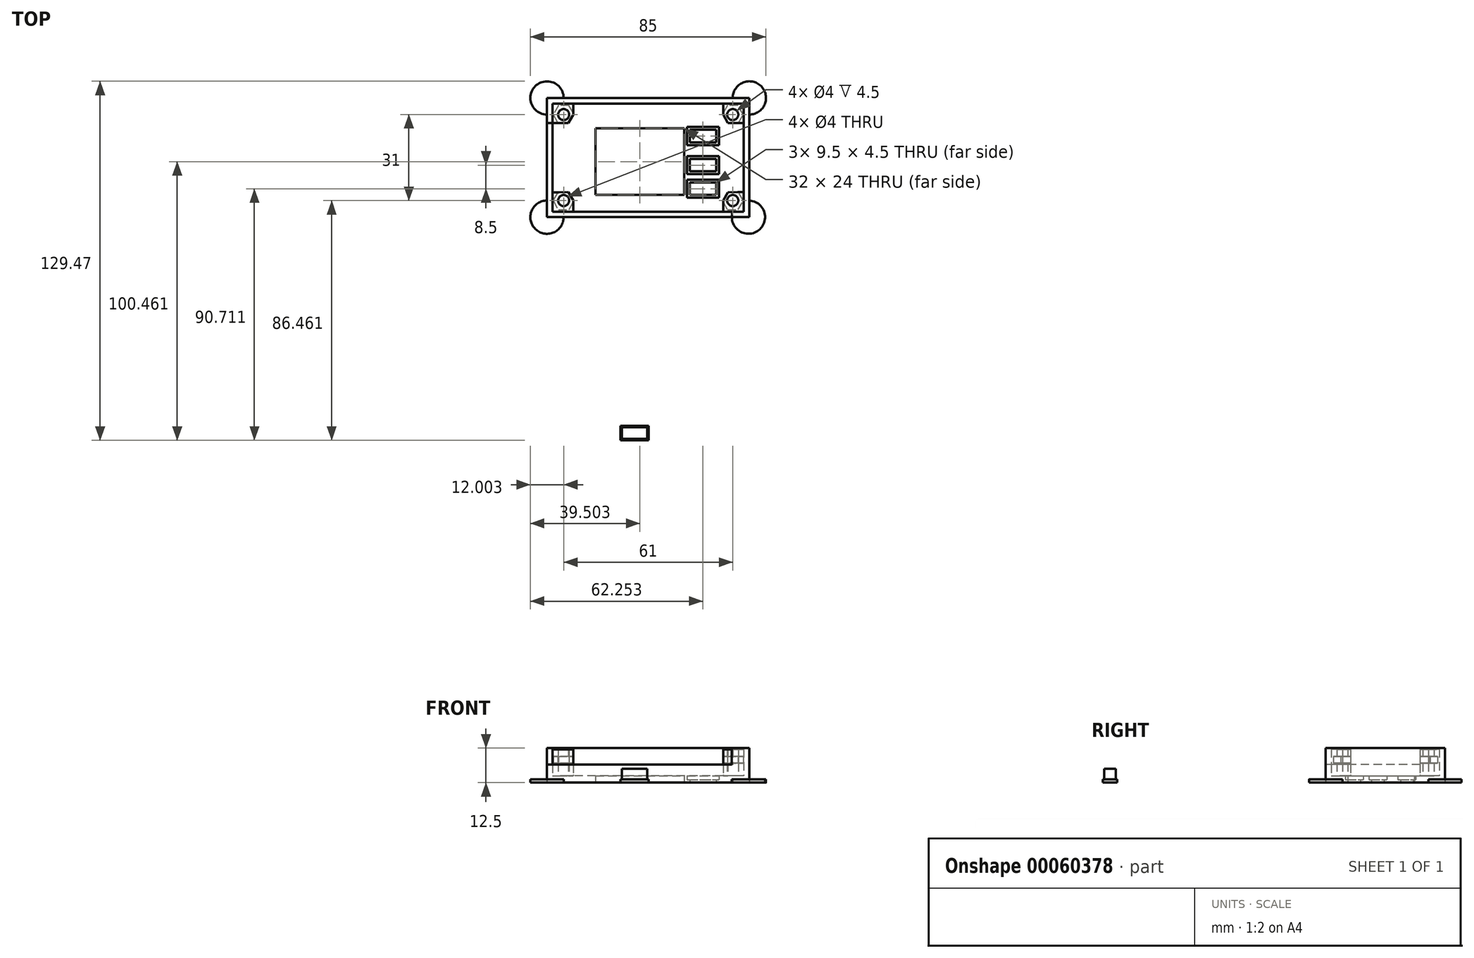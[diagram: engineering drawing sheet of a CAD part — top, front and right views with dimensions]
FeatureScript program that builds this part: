
annotation { "Feature Type Name" : "Feature", "Feature Type Description" : "" }
export const myFeature = defineFeature(function(context is Context, id is Id, definition is map)
    precondition{}
    {
        {
            var Q0;
            Q0=qCreatedBy(makeId("Top.planeOp"),FACE);
            var sketch = newSketch(context, id + "F0", { "sketchPlane" : qUnion([Q0])});
            skCircle(sketch, "E0.cCircle", {"center": v(0, 0) * mm, "radius": 3 * mm, "construction": true});
            skLineSegment(sketch, "E0.0", {"start": v(1.73, 3) * mm, "end": v(3.46, 0) * mm});
            skLineSegment(sketch, "E0.1", {"start": v(3.46, 0) * mm, "end": v(1.74, -3) * mm});
            skLineSegment(sketch, "E0.2", {"start": v(1.74, -3) * mm, "end": v(-1.73, -3) * mm});
            skLineSegment(sketch, "E0.3", {"start": v(-1.73, -3) * mm, "end": v(-3.46, 0) * mm});
            skLineSegment(sketch, "E0.4", {"start": v(-3.46, 0) * mm, "end": v(-1.74, 3) * mm});
            skLineSegment(sketch, "E0.5", {"start": v(-1.74, 3) * mm, "end": v(1.73, 3) * mm});
            skPoint(sketch, "E0.0.midPoint", {"position": v(2.6, 1.5) * mm});
            skCircle(sketch, "E1", {"center": v(0, 0) * mm, "radius": 1.5 * mm});
            skLineSegment(sketch, "E2.bottom", {"start": v(-12.76, 68.41) * mm, "end": v(56.24, 68.41) * mm});
            skLineSegment(sketch, "E2.top", {"start": v(-12.76, 29.41) * mm, "end": v(56.24, 29.41) * mm});
            skLineSegment(sketch, "E2.left", {"start": v(-12.76, 68.41) * mm, "end": v(-12.76, 29.41) * mm});
            skLineSegment(sketch, "E2.right", {"start": v(56.24, 68.41) * mm, "end": v(56.24, 29.41) * mm});
            skPoint(sketch, "E3.0.midPoint", {"position": v(-6.16, 65.92) * mm});
            skLineSegment(sketch, "E3.3", {"start": v(-10.48, 61.4) * mm, "end": v(-12.22, 64.4) * mm, "construction": true});
            skLineSegment(sketch, "E3.2", {"start": v(-7.02, 61.41) * mm, "end": v(-10.48, 61.4) * mm});
            skLineSegment(sketch, "E3.1", {"start": v(-5.3, 64.42) * mm, "end": v(-7.02, 61.41) * mm});
            skLineSegment(sketch, "E3.0", {"start": v(-7.03, 67.41) * mm, "end": v(-5.3, 64.42) * mm, "construction": true});
            skLineSegment(sketch, "E3.4", {"start": v(-12.22, 64.4) * mm, "end": v(-10.5, 67.4) * mm, "construction": true});
            skLineSegment(sketch, "E3.5", {"start": v(-10.5, 67.4) * mm, "end": v(-7.03, 67.41) * mm, "construction": true});
            skCircle(sketch, "E4", {"center": v(-8.76, 64.41) * mm, "radius": 1.5 * mm, "construction": true});
            skCircle(sketch, "E3.cCircle", {"center": v(-8.76, 64.41) * mm, "radius": 3 * mm, "construction": true});
            skPoint(sketch, "E5.0.midPoint", {"position": v(-6.16, 34.92) * mm});
            skLineSegment(sketch, "E5.3", {"start": v(-10.48, 30.4) * mm, "end": v(-12.22, 33.4) * mm, "construction": true});
            skLineSegment(sketch, "E5.2", {"start": v(-7.02, 30.41) * mm, "end": v(-10.48, 30.4) * mm, "construction": true});
            skLineSegment(sketch, "E5.1", {"start": v(-5.3, 33.42) * mm, "end": v(-7.02, 30.41) * mm, "construction": true});
            skLineSegment(sketch, "E5.0", {"start": v(-7.03, 36.41) * mm, "end": v(-5.3, 33.42) * mm});
            skLineSegment(sketch, "E5.4", {"start": v(-12.22, 33.4) * mm, "end": v(-10.5, 36.4) * mm, "construction": true});
            skLineSegment(sketch, "E5.5", {"start": v(-10.5, 36.4) * mm, "end": v(-7.03, 36.41) * mm});
            skCircle(sketch, "E6", {"center": v(-8.76, 33.41) * mm, "radius": 1.5 * mm, "construction": true});
            skCircle(sketch, "E5.cCircle", {"center": v(-8.76, 33.41) * mm, "radius": 3 * mm, "construction": true});
            skPoint(sketch, "E7.0.midPoint", {"position": v(54.84, 65.92) * mm});
            skLineSegment(sketch, "E7.3", {"start": v(50.52, 61.4) * mm, "end": v(48.78, 64.4) * mm});
            skLineSegment(sketch, "E7.2", {"start": v(53.98, 61.41) * mm, "end": v(50.52, 61.4) * mm});
            skLineSegment(sketch, "E7.1", {"start": v(55.7, 64.42) * mm, "end": v(53.98, 61.41) * mm, "construction": true});
            skLineSegment(sketch, "E7.0", {"start": v(53.97, 67.41) * mm, "end": v(55.7, 64.42) * mm, "construction": true});
            skLineSegment(sketch, "E7.4", {"start": v(48.78, 64.4) * mm, "end": v(50.5, 67.4) * mm, "construction": true});
            skLineSegment(sketch, "E7.5", {"start": v(50.5, 67.4) * mm, "end": v(53.97, 67.41) * mm, "construction": true});
            skCircle(sketch, "E8", {"center": v(52.24, 64.41) * mm, "radius": 1.5 * mm, "construction": true});
            skCircle(sketch, "E7.cCircle", {"center": v(52.24, 64.41) * mm, "radius": 3 * mm, "construction": true});
            skPoint(sketch, "E9.0.midPoint", {"position": v(54.84, 34.92) * mm});
            skLineSegment(sketch, "E9.3", {"start": v(50.52, 30.4) * mm, "end": v(48.78, 33.4) * mm, "construction": true});
            skLineSegment(sketch, "E9.2", {"start": v(53.98, 30.41) * mm, "end": v(50.52, 30.4) * mm, "construction": true});
            skLineSegment(sketch, "E9.1", {"start": v(55.7, 33.42) * mm, "end": v(53.98, 30.41) * mm, "construction": true});
            skLineSegment(sketch, "E9.0", {"start": v(53.97, 36.41) * mm, "end": v(55.7, 33.42) * mm, "construction": true});
            skLineSegment(sketch, "E9.4", {"start": v(48.78, 33.4) * mm, "end": v(50.5, 36.4) * mm});
            skLineSegment(sketch, "E9.5", {"start": v(50.5, 36.4) * mm, "end": v(53.97, 36.41) * mm});
            skCircle(sketch, "E10", {"center": v(52.24, 33.41) * mm, "radius": 1.5 * mm, "construction": true});
            skCircle(sketch, "E9.cCircle", {"center": v(52.24, 33.41) * mm, "radius": 3 * mm, "construction": true});
            skLineSegment(sketch, "E11", {"start": v(48.78, 33.4) * mm, "end": v(48.78, 29.41) * mm});
            skLineSegment(sketch, "E12", {"start": v(53.97, 36.41) * mm, "end": v(56.24, 36.41) * mm});
            skCircle(sketch, "E13.0", {"center": v(52.24, 33.41) * mm, "radius": 2 * mm});
            skLineSegment(sketch, "E14.0", {"start": v(50.34, 30.1) * mm, "end": v(48.52, 33.25) * mm});
            skLineSegment(sketch, "E14.1", {"start": v(54.15, 30.11) * mm, "end": v(50.34, 30.1) * mm});
            skLineSegment(sketch, "E14.2", {"start": v(56.05, 33.42) * mm, "end": v(54.15, 30.11) * mm});
            skLineSegment(sketch, "E14.3", {"start": v(54.23, 36.56) * mm, "end": v(56.05, 33.42) * mm});
            skLineSegment(sketch, "E15", {"start": v(-5.3, 33.42) * mm, "end": v(-5.3, 29.41) * mm});
            skLineSegment(sketch, "E16", {"start": v(-10.5, 36.4) * mm, "end": v(-12.76, 36.4) * mm});
            skLineSegment(sketch, "E17", {"start": v(-10.48, 61.4) * mm, "end": v(-12.76, 61.4) * mm});
            skLineSegment(sketch, "E18", {"start": v(-5.3, 64.42) * mm, "end": v(-5.3, 68.41) * mm});
            skLineSegment(sketch, "E19", {"start": v(53.98, 61.41) * mm, "end": v(56.24, 61.42) * mm});
            skLineSegment(sketch, "E20", {"start": v(48.78, 64.4) * mm, "end": v(48.78, 68.41) * mm});
            skCircle(sketch, "E21.0", {"center": v(52.24, 64.41) * mm, "radius": 2 * mm});
            skCircle(sketch, "E22.0", {"center": v(-8.76, 64.41) * mm, "radius": 2 * mm});
            skCircle(sketch, "E23.0", {"center": v(-8.76, 33.41) * mm, "radius": 2 * mm});
            skLineSegment(sketch, "E24.0", {"start": v(-6.86, 67.71) * mm, "end": v(-5.03, 64.57) * mm});
            skLineSegment(sketch, "E24.1", {"start": v(-10.67, 67.7) * mm, "end": v(-6.86, 67.71) * mm});
            skLineSegment(sketch, "E24.2", {"start": v(-12.57, 64.4) * mm, "end": v(-10.67, 67.7) * mm});
            skLineSegment(sketch, "E24.3", {"start": v(-10.74, 61.26) * mm, "end": v(-12.57, 64.4) * mm});
            skLineSegment(sketch, "E25.0", {"start": v(-12.57, 33.4) * mm, "end": v(-10.76, 36.56) * mm});
            skLineSegment(sketch, "E25.1", {"start": v(-10.66, 30.1) * mm, "end": v(-12.57, 33.4) * mm});
            skLineSegment(sketch, "E25.2", {"start": v(-6.85, 30.11) * mm, "end": v(-10.66, 30.1) * mm});
            skLineSegment(sketch, "E25.3", {"start": v(-5.03, 33.27) * mm, "end": v(-6.85, 30.11) * mm});
            skLineSegment(sketch, "E26.0", {"start": v(56.05, 64.42) * mm, "end": v(50.35, 54.5) * mm});
            skLineSegment(sketch, "E26.1", {"start": v(54.14, 67.71) * mm, "end": v(56.05, 64.42) * mm});
            skLineSegment(sketch, "E26.2", {"start": v(50.33, 67.7) * mm, "end": v(54.14, 67.71) * mm});
            skLineSegment(sketch, "E26.3", {"start": v(48.52, 64.55) * mm, "end": v(50.33, 67.7) * mm});
            skPoint(sketch, "E27", {"position": v(2.74, 35.41) * mm});
            skLineSegment(sketch, "E28.bottom", {"start": v(2.74, 35.41) * mm, "end": v(34.74, 35.41) * mm});
            skLineSegment(sketch, "E28.top", {"start": v(2.74, 59.41) * mm, "end": v(34.74, 59.41) * mm});
            skLineSegment(sketch, "E28.left", {"start": v(2.74, 35.41) * mm, "end": v(2.74, 59.41) * mm});
            skLineSegment(sketch, "E28.right", {"start": v(34.74, 35.41) * mm, "end": v(34.74, 59.41) * mm});
            skPoint(sketch, "E29", {"position": v(36.74, 59.41) * mm});
            skLineSegment(sketch, "E30.bottom", {"start": v(36.74, 59.41) * mm, "end": v(46.24, 59.41) * mm, "construction": true});
            skLineSegment(sketch, "E30.top", {"start": v(36.74, 54.91) * mm, "end": v(46.24, 54.91) * mm, "construction": true});
            skLineSegment(sketch, "E30.left", {"start": v(36.74, 59.41) * mm, "end": v(36.74, 54.91) * mm, "construction": true});
            skLineSegment(sketch, "E30.right", {"start": v(46.24, 59.41) * mm, "end": v(46.24, 54.91) * mm, "construction": true});
            skLineSegment(sketch, "E31.bottom", {"start": v(36.74, 35.41) * mm, "end": v(46.24, 35.41) * mm});
            skLineSegment(sketch, "E31.top", {"start": v(36.74, 39.91) * mm, "end": v(46.24, 39.91) * mm});
            skLineSegment(sketch, "E31.left", {"start": v(36.74, 35.41) * mm, "end": v(36.74, 39.91) * mm});
            skLineSegment(sketch, "E31.right", {"start": v(46.24, 35.41) * mm, "end": v(46.24, 39.91) * mm});
            skLineSegment(sketch, "E32.bottom", {"start": v(36.74, 43.91) * mm, "end": v(46.24, 43.91) * mm});
            skLineSegment(sketch, "E32.top", {"start": v(36.74, 48.41) * mm, "end": v(46.24, 48.41) * mm});
            skLineSegment(sketch, "E32.left", {"start": v(36.74, 43.91) * mm, "end": v(36.74, 48.41) * mm});
            skLineSegment(sketch, "E32.right", {"start": v(46.24, 43.91) * mm, "end": v(46.24, 48.41) * mm});
            skLineSegment(sketch, "E33.0", {"start": v(-14.76, 70.41) * mm, "end": v(-14.76, 27.41) * mm});
            skLineSegment(sketch, "E33.1", {"start": v(-14.76, 70.41) * mm, "end": v(58.24, 70.41) * mm});
            skLineSegment(sketch, "E33.2", {"start": v(58.24, 70.41) * mm, "end": v(58.24, 27.41) * mm});
            skLineSegment(sketch, "E33.3", {"start": v(-14.76, 27.41) * mm, "end": v(58.24, 27.41) * mm});
            skPoint(sketch, "E34", {"position": v(-14.76, 61.41) * mm});
            skLineSegment(sketch, "E35", {"start": v(-14.76, 61.41) * mm, "end": v(-12.76, 61.41) * mm});
            skLineSegment(sketch, "E36.bottom", {"start": v(13.09, -34.33) * mm, "end": v(22.29, -34.33) * mm});
            skLineSegment(sketch, "E36.top", {"start": v(13.09, -38.53) * mm, "end": v(22.29, -38.53) * mm});
            skLineSegment(sketch, "E36.left", {"start": v(13.09, -34.33) * mm, "end": v(13.09, -38.53) * mm});
            skLineSegment(sketch, "E36.right", {"start": v(22.29, -34.33) * mm, "end": v(22.29, -38.53) * mm});
            skLineSegment(sketch, "E37.0", {"start": v(12.09, -33.33) * mm, "end": v(23.29, -33.33) * mm});
            skLineSegment(sketch, "E37.1", {"start": v(12.09, -33.33) * mm, "end": v(12.09, -39.53) * mm});
            skLineSegment(sketch, "E37.2", {"start": v(12.09, -39.53) * mm, "end": v(23.29, -39.53) * mm});
            skLineSegment(sketch, "E37.3", {"start": v(23.29, -33.33) * mm, "end": v(23.29, -39.53) * mm});
            skLineSegment(sketch, "E38.bottom", {"start": v(12.2, -48.35) * mm, "end": v(21.4, -48.35) * mm});
            skLineSegment(sketch, "E38.top", {"start": v(12.2, -52.55) * mm, "end": v(21.4, -52.55) * mm});
            skLineSegment(sketch, "E38.left", {"start": v(12.2, -48.35) * mm, "end": v(12.2, -52.55) * mm});
            skLineSegment(sketch, "E38.right", {"start": v(21.4, -48.35) * mm, "end": v(21.4, -52.55) * mm});
            skLineSegment(sketch, "E39.0", {"start": v(11.7, -47.85) * mm, "end": v(21.9, -47.85) * mm});
            skLineSegment(sketch, "E39.1", {"start": v(11.7, -47.85) * mm, "end": v(11.7, -53.05) * mm});
            skLineSegment(sketch, "E39.2", {"start": v(11.7, -53.05) * mm, "end": v(21.9, -53.05) * mm});
            skLineSegment(sketch, "E39.3", {"start": v(21.9, -47.85) * mm, "end": v(21.9, -53.05) * mm});
            skArc(sketch, "E40", {"start": v(58.24, 64.42) * mm, "mid": v(62.48, 74.66) * mm, "end": v(52.24, 70.41) * mm});
            skArc(sketch, "E41", {"start": v(52.24, 29.41) * mm, "mid": v(61.24, 22.44) * mm, "end": v(58.24, 33.42) * mm});
            skArc(sketch, "E42", {"start": v(-14.76, 33.4) * mm, "mid": v(-19, 23.16) * mm, "end": v(-8.76, 27.41) * mm});
            skArc(sketch, "E43", {"start": v(-8.76, 70.41) * mm, "mid": v(-19, 74.64) * mm, "end": v(-14.76, 64.4) * mm});
            skLineSegment(sketch, "E44.0", {"start": v(35.74, 53.91) * mm, "end": v(47.24, 53.91) * mm, "construction": true});
            skLineSegment(sketch, "E44.1", {"start": v(35.74, 60.41) * mm, "end": v(35.74, 53.91) * mm, "construction": true});
            skLineSegment(sketch, "E44.2", {"start": v(35.74, 60.41) * mm, "end": v(47.24, 60.41) * mm, "construction": true});
            skLineSegment(sketch, "E44.3", {"start": v(47.24, 60.41) * mm, "end": v(47.24, 53.91) * mm, "construction": true});
            skLineSegment(sketch, "E45.0", {"start": v(35.74, 49.41) * mm, "end": v(47.24, 49.41) * mm});
            skLineSegment(sketch, "E45.1", {"start": v(35.74, 42.91) * mm, "end": v(35.74, 49.41) * mm});
            skLineSegment(sketch, "E45.2", {"start": v(35.74, 42.91) * mm, "end": v(47.24, 42.91) * mm});
            skLineSegment(sketch, "E45.3", {"start": v(47.24, 42.91) * mm, "end": v(47.24, 49.41) * mm});
            skLineSegment(sketch, "E46.0", {"start": v(35.74, 40.91) * mm, "end": v(47.24, 40.91) * mm});
            skLineSegment(sketch, "E46.1", {"start": v(35.74, 34.41) * mm, "end": v(35.74, 40.91) * mm});
            skLineSegment(sketch, "E46.2", {"start": v(35.74, 34.41) * mm, "end": v(47.24, 34.41) * mm});
            skLineSegment(sketch, "E46.3", {"start": v(47.24, 34.41) * mm, "end": v(47.24, 40.91) * mm});
            skLineSegment(sketch, "E47.bottom", {"start": v(36.74, 54.41) * mm, "end": v(46.24, 54.41) * mm});
            skLineSegment(sketch, "E47.top", {"start": v(36.74, 58.91) * mm, "end": v(46.24, 58.91) * mm});
            skLineSegment(sketch, "E47.left", {"start": v(36.74, 54.41) * mm, "end": v(36.74, 58.91) * mm});
            skLineSegment(sketch, "E47.right", {"start": v(46.24, 54.41) * mm, "end": v(46.24, 58.91) * mm});
            skLineSegment(sketch, "E48.0", {"start": v(35.74, 59.91) * mm, "end": v(47.24, 59.91) * mm});
            skLineSegment(sketch, "E48.1", {"start": v(35.74, 53.41) * mm, "end": v(35.74, 59.91) * mm});
            skLineSegment(sketch, "E48.2", {"start": v(35.74, 53.41) * mm, "end": v(47.24, 53.41) * mm});
            skLineSegment(sketch, "E48.3", {"start": v(47.24, 53.41) * mm, "end": v(47.24, 59.91) * mm});
            skSolve(sketch);
        }
        {
            var Q0;
            {var subQ14=sQuery(id+"F0.wireOp",EDGE,"E3.2");Q0=makeQuery(id+"F0.imprint","IMPRINT",FACE,{"disambiguationData":[TD([[makeQuery(id+"F0.imprint","IMPRINT",EDGE,{"derivedFrom":subQ14}),1.0]])]});}
            var Q1;
            Q1=makeQuery(id+"F0.imprint","IMPRINT",FACE,{"disambiguationData":[TD([[makeQuery(id+"F0.imprint","IMPRINT",EDGE,{"derivedFrom":sQuery(id+"F0.wireOp",EDGE,"E22.0")}),1.0]])]});
            var Q2;
            Q2=makeQuery(id+"F0.imprint","IMPRINT",FACE,{"disambiguationData":[TD([[makeQuery(id+"F0.imprint","IMPRINT",EDGE,{"derivedFrom":sQuery(id+"F0.wireOp",EDGE,"E21.0")}),1.0]])]});
            var Q3;
            Q3=makeQuery(id+"F0.imprint","IMPRINT",FACE,{"disambiguationData":[TD([[makeQuery(id+"F0.imprint","IMPRINT",EDGE,{"derivedFrom":sQuery(id+"F0.wireOp",EDGE,"E13.0")}),1.0]])]});
            var Q4;
            Q4=makeQuery(id+"F0.imprint","IMPRINT",FACE,{"disambiguationData":[TD([[makeQuery(id+"F0.imprint","IMPRINT",EDGE,{"derivedFrom":sQuery(id+"F0.wireOp",EDGE,"E23.0")}),1.0]])]});
            var Q5;
            {var subQ12=sQuery(id+"F0.wireOp",EDGE,"E25.1");Q5=makeQuery(id+"F0.imprint","IMPRINT",FACE,{"disambiguationData":[TD([[makeQuery(id+"F0.imprint","IMPRINT",EDGE,{"derivedFrom":subQ12}),1.0]])]});}
            var Q6;
            {var subQ1=sQuery(id+"F0.wireOp",EDGE,"E5.0");Q6=makeQuery(id+"F0.imprint","IMPRINT",FACE,{"disambiguationData":[TD([[makeQuery(id+"F0.imprint","IMPRINT",EDGE,{"derivedFrom":subQ1}),-1.0]])]});}
            var Q7;
            {var subQ0=sQuery(id+"F0.wireOp",EDGE,"E35");Q7=makeQuery(id+"F0.imprint","IMPRINT",FACE,{"disambiguationData":[TD([[makeQuery(id+"F0.imprint","IMPRINT",EDGE,{"derivedFrom":subQ0}),-1.0]])]});}
            var Q8;
            {var subQ0=sQuery(id+"F0.wireOp",EDGE,"E35");Q8=makeQuery(id+"F0.imprint","IMPRINT",FACE,{"disambiguationData":[TD([[makeQuery(id+"F0.imprint","IMPRINT",EDGE,{"derivedFrom":subQ0}),-1.0]])]});}
            var Q9;
            {var subQ12=sQuery(id+"F0.wireOp",EDGE,"E24.1");Q9=makeQuery(id+"F0.imprint","IMPRINT",FACE,{"disambiguationData":[TD([[makeQuery(id+"F0.imprint","IMPRINT",EDGE,{"derivedFrom":subQ12}),1.0]])]});}
            var Q10;
            {var subQ6=sQuery(id+"F0.wireOp",EDGE,"E3.2");Q10=makeQuery(id+"F0.imprint","IMPRINT",FACE,{"disambiguationData":[TD([[makeQuery(id+"F0.imprint","IMPRINT",EDGE,{"derivedFrom":subQ6}),-1.0]])]});}
            var Q11;
            {var subQ13=sQuery(id+"F0.wireOp",EDGE,"E14.1");Q11=makeQuery(id+"F0.imprint","IMPRINT",FACE,{"disambiguationData":[TD([[makeQuery(id+"F0.imprint","IMPRINT",EDGE,{"derivedFrom":subQ13}),1.0]])]});}
            var Q12;
            {var subQ5=sQuery(id+"F0.wireOp",EDGE,"E26.1");Q12=makeQuery(id+"F0.imprint","IMPRINT",FACE,{"disambiguationData":[TD([[makeQuery(id+"F0.imprint","IMPRINT",EDGE,{"derivedFrom":subQ5}),1.0]])]});}
            var Q13;
            {var subQ1=sQuery(id+"F0.wireOp",EDGE,"E7.3");Q13=makeQuery(id+"F0.imprint","IMPRINT",FACE,{"disambiguationData":[TD([[makeQuery(id+"F0.imprint","IMPRINT",EDGE,{"derivedFrom":subQ1}),-1.0]])]});}
            var Q14;
            {var subQ17=sQuery(id+"F0.wireOp",EDGE,"E35");Q14=makeQuery(id+"F0.imprint","IMPRINT",FACE,{"disambiguationData":[TD([[makeQuery(id+"F0.imprint","IMPRINT",EDGE,{"derivedFrom":subQ17}),1.0]])]});}
            var Q15;
            {var subQ4=sQuery(id+"F0.wireOp",EDGE,"E9.4");Q15=makeQuery(id+"F0.imprint","IMPRINT",FACE,{"disambiguationData":[TD([[makeQuery(id+"F0.imprint","IMPRINT",EDGE,{"derivedFrom":subQ4}),-1.0]])]});}
            extrude(context, id + "F1", {"entities" : qUnion([Q0, Q1, Q2, Q3, Q4, Q5, Q6, Q7, Q8, Q9, Q10, Q11, Q12, Q13, Q14, Q15]), "depth" : 2.5 * mm});
        }
        {
            var Q0;
            Q0=makeQuery(id+"F0.imprint","IMPRINT",FACE,{"disambiguationData":[TD([[makeQuery(id+"F0.imprint","IMPRINT",EDGE,{"derivedFrom":sQuery(id+"F0.wireOp",EDGE,"E30.bottom")}),1.0]])]});
            var Q1;
            Q1=makeQuery(id+"F0.imprint","IMPRINT",FACE,{"disambiguationData":[TD([[makeQuery(id+"F0.imprint","IMPRINT",EDGE,{"derivedFrom":sQuery(id+"F0.wireOp",EDGE,"E32.bottom")}),-1.0]])]});
            var Q2;
            Q2=makeQuery(id+"F0.imprint","IMPRINT",FACE,{"disambiguationData":[TD([[makeQuery(id+"F0.imprint","IMPRINT",EDGE,{"derivedFrom":sQuery(id+"F0.wireOp",EDGE,"E31.bottom")}),-1.0]])]});
            var Q3;
            Q3=makeQuery(id+"F0.imprint","IMPRINT",FACE,{"disambiguationData":[TD([[makeQuery(id+"F0.imprint","IMPRINT",EDGE,{"derivedFrom":sQuery(id+"F0.wireOp",EDGE,"E47.bottom")}),-1.0]])]});
            extrude(context, id + "F2", {"entities" : qUnion([Q0, Q1, Q2, Q3]), "operationType" : NewBodyOperationType.ADD, "depth" : 1 * mm});
        }
        {
            var Q0;
            {var subQ12=sQuery(id+"F0.wireOp",EDGE,"E14.1");Q0=makeQuery(id+"F0.imprint","IMPRINT",FACE,{"disambiguationData":[TD([[makeQuery(id+"F0.imprint","IMPRINT",EDGE,{"derivedFrom":subQ12}),1.0]])]});}
            var Q1;
            {var subQ6=sQuery(id+"F0.wireOp",EDGE,"E9.4");Q1=makeQuery(id+"F0.imprint","IMPRINT",FACE,{"disambiguationData":[TD([[makeQuery(id+"F0.imprint","IMPRINT",EDGE,{"derivedFrom":subQ6}),-1.0]])]});}
            var Q2;
            {var subQ5=sQuery(id+"F0.wireOp",EDGE,"E25.1");Q2=makeQuery(id+"F0.imprint","IMPRINT",FACE,{"disambiguationData":[TD([[makeQuery(id+"F0.imprint","IMPRINT",EDGE,{"derivedFrom":subQ5}),1.0]])]});}
            var Q3;
            {var subQ5=sQuery(id+"F0.wireOp",EDGE,"E5.0");Q3=makeQuery(id+"F0.imprint","IMPRINT",FACE,{"disambiguationData":[TD([[makeQuery(id+"F0.imprint","IMPRINT",EDGE,{"derivedFrom":subQ5}),-1.0]])]});}
            var Q4;
            {var subQ11=sQuery(id+"F0.wireOp",EDGE,"E24.1");Q4=makeQuery(id+"F0.imprint","IMPRINT",FACE,{"disambiguationData":[TD([[makeQuery(id+"F0.imprint","IMPRINT",EDGE,{"derivedFrom":subQ11}),1.0]])]});}
            var Q5;
            {var subQ5=sQuery(id+"F0.wireOp",EDGE,"E3.2");Q5=makeQuery(id+"F0.imprint","IMPRINT",FACE,{"disambiguationData":[TD([[makeQuery(id+"F0.imprint","IMPRINT",EDGE,{"derivedFrom":subQ5}),-1.0]])]});}
            var Q6;
            {var subQ7=sQuery(id+"F0.wireOp",EDGE,"E26.1");Q6=makeQuery(id+"F0.imprint","IMPRINT",FACE,{"disambiguationData":[TD([[makeQuery(id+"F0.imprint","IMPRINT",EDGE,{"derivedFrom":subQ7}),1.0]])]});}
            var Q7;
            {var subQ1=sQuery(id+"F0.wireOp",EDGE,"E7.3");Q7=makeQuery(id+"F0.imprint","IMPRINT",FACE,{"disambiguationData":[TD([[makeQuery(id+"F0.imprint","IMPRINT",EDGE,{"derivedFrom":subQ1}),-1.0]])]});}
            extrude(context, id + "F3", {"entities" : qUnion([Q0, Q1, Q2, Q3, Q4, Q5, Q6, Q7]), "operationType" : NewBodyOperationType.ADD, "depth" : 7 * mm});
        }
        {
            var Q0;
            {var subQ12=sQuery(id+"F0.wireOp",EDGE,"E14.1");Q0=makeQuery(id+"F0.imprint","IMPRINT",FACE,{"disambiguationData":[TD([[makeQuery(id+"F0.imprint","IMPRINT",EDGE,{"derivedFrom":subQ12}),1.0]])]});}
            var Q1;
            {var subQ7=sQuery(id+"F0.wireOp",EDGE,"E26.1");Q1=makeQuery(id+"F0.imprint","IMPRINT",FACE,{"disambiguationData":[TD([[makeQuery(id+"F0.imprint","IMPRINT",EDGE,{"derivedFrom":subQ7}),1.0]])]});}
            var Q2;
            {var subQ11=sQuery(id+"F0.wireOp",EDGE,"E24.1");Q2=makeQuery(id+"F0.imprint","IMPRINT",FACE,{"disambiguationData":[TD([[makeQuery(id+"F0.imprint","IMPRINT",EDGE,{"derivedFrom":subQ11}),1.0]])]});}
            var Q3;
            {var subQ5=sQuery(id+"F0.wireOp",EDGE,"E25.1");Q3=makeQuery(id+"F0.imprint","IMPRINT",FACE,{"disambiguationData":[TD([[makeQuery(id+"F0.imprint","IMPRINT",EDGE,{"derivedFrom":subQ5}),1.0]])]});}
            extrude(context, id + "F4", {"entities" : qUnion([Q0, Q1, Q2, Q3]), "operationType" : NewBodyOperationType.ADD, "endBound" : BoundingType.UP_TO_NEXT, "depth" : 25 * mm});
        }
        {
            var Q0;
            Q0=makeQuery(id+"F4.opExtrude","CAP_FACE",FACE,{"disambiguationData":[OSD([sQuery(id+"F0.wireOp",EDGE,"E2.top"),sQuery(id+"F0.wireOp",EDGE,"E2.right"),sQuery(id+"F0.wireOp",EDGE,"E9.4"),sQuery(id+"F0.wireOp",EDGE,"E9.5"),sQuery(id+"F0.wireOp",EDGE,"E11"),sQuery(id+"F0.wireOp",EDGE,"E12"),sQuery(id+"F0.wireOp",EDGE,"E13.0")])],"isStart":false});
            var Q1;
            Q1=makeQuery(id+"F4.opExtrude","CAP_FACE",FACE,{"disambiguationData":[OSD([sQuery(id+"F0.wireOp",EDGE,"E2.top"),sQuery(id+"F0.wireOp",EDGE,"E2.left"),sQuery(id+"F0.wireOp",EDGE,"E5.0"),sQuery(id+"F0.wireOp",EDGE,"E5.5"),sQuery(id+"F0.wireOp",EDGE,"E15"),sQuery(id+"F0.wireOp",EDGE,"E16"),sQuery(id+"F0.wireOp",EDGE,"E23.0")])],"isStart":false});
            var Q2;
            Q2=makeQuery(id+"F4.opExtrude","CAP_FACE",FACE,{"disambiguationData":[OSD([sQuery(id+"F0.wireOp",EDGE,"E2.bottom"),sQuery(id+"F0.wireOp",EDGE,"E2.left"),sQuery(id+"F0.wireOp",EDGE,"E3.2"),sQuery(id+"F0.wireOp",EDGE,"E3.1"),sQuery(id+"F0.wireOp",EDGE,"E17"),sQuery(id+"F0.wireOp",EDGE,"E18"),sQuery(id+"F0.wireOp",EDGE,"E22.0")])],"isStart":false});
            var Q3;
            Q3=makeQuery(id+"F4.opExtrude","CAP_FACE",FACE,{"disambiguationData":[OSD([sQuery(id+"F0.wireOp",EDGE,"E2.bottom"),sQuery(id+"F0.wireOp",EDGE,"E2.right"),sQuery(id+"F0.wireOp",EDGE,"E7.3"),sQuery(id+"F0.wireOp",EDGE,"E7.2"),sQuery(id+"F0.wireOp",EDGE,"E19"),sQuery(id+"F0.wireOp",EDGE,"E20"),sQuery(id+"F0.wireOp",EDGE,"E21.0")])],"isStart":false});
            var Q4;
            {var subQ13=sQuery(id+"F0.wireOp",EDGE,"E14.1");Q4=makeQuery(id+"F0.imprint","IMPRINT",FACE,{"disambiguationData":[TD([[makeQuery(id+"F0.imprint","IMPRINT",EDGE,{"derivedFrom":subQ13}),1.0]])]});}
            var Q5;
            {var subQ5=sQuery(id+"F0.wireOp",EDGE,"E26.1");Q5=makeQuery(id+"F0.imprint","IMPRINT",FACE,{"disambiguationData":[TD([[makeQuery(id+"F0.imprint","IMPRINT",EDGE,{"derivedFrom":subQ5}),1.0]])]});}
            var Q6;
            {var subQ12=sQuery(id+"F0.wireOp",EDGE,"E24.1");Q6=makeQuery(id+"F0.imprint","IMPRINT",FACE,{"disambiguationData":[TD([[makeQuery(id+"F0.imprint","IMPRINT",EDGE,{"derivedFrom":subQ12}),1.0]])]});}
            var Q7;
            {var subQ12=sQuery(id+"F0.wireOp",EDGE,"E25.1");Q7=makeQuery(id+"F0.imprint","IMPRINT",FACE,{"disambiguationData":[TD([[makeQuery(id+"F0.imprint","IMPRINT",EDGE,{"derivedFrom":subQ12}),1.0]])]});}
            extrude(context, id + "F5", {"entities" : qUnion([Q0, Q1, Q2, Q3, Q4, Q5, Q6, Q7]), "operationType" : NewBodyOperationType.ADD, "depth" : 12 * mm});
        }
        {
            var Q0;
            Q0=makeQuery(id+"F3.opExtrude","CAP_FACE",FACE,{"disambiguationData":[OSD([sQuery(id+"F0.wireOp",EDGE,"E2.top"),sQuery(id+"F0.wireOp",EDGE,"E2.right"),sQuery(id+"F0.wireOp",EDGE,"E9.4"),sQuery(id+"F0.wireOp",EDGE,"E9.5"),sQuery(id+"F0.wireOp",EDGE,"E11"),sQuery(id+"F0.wireOp",EDGE,"E12"),sQuery(id+"F0.wireOp",EDGE,"E13.0")])],"isStart":false});
            var Q1;
            Q1=makeQuery(id+"F3.opExtrude","CAP_FACE",FACE,{"disambiguationData":[OSD([sQuery(id+"F0.wireOp",EDGE,"E2.top"),sQuery(id+"F0.wireOp",EDGE,"E2.left"),sQuery(id+"F0.wireOp",EDGE,"E5.0"),sQuery(id+"F0.wireOp",EDGE,"E5.5"),sQuery(id+"F0.wireOp",EDGE,"E15"),sQuery(id+"F0.wireOp",EDGE,"E16"),sQuery(id+"F0.wireOp",EDGE,"E23.0")])],"isStart":false});
            var Q2;
            Q2=makeQuery(id+"F3.opExtrude","CAP_FACE",FACE,{"disambiguationData":[OSD([sQuery(id+"F0.wireOp",EDGE,"E2.bottom"),sQuery(id+"F0.wireOp",EDGE,"E2.left"),sQuery(id+"F0.wireOp",EDGE,"E3.2"),sQuery(id+"F0.wireOp",EDGE,"E3.1"),sQuery(id+"F0.wireOp",EDGE,"E17"),sQuery(id+"F0.wireOp",EDGE,"E18"),sQuery(id+"F0.wireOp",EDGE,"E22.0")])],"isStart":false});
            var Q3;
            Q3=makeQuery(id+"F3.opExtrude","CAP_FACE",FACE,{"disambiguationData":[OSD([sQuery(id+"F0.wireOp",EDGE,"E2.bottom"),sQuery(id+"F0.wireOp",EDGE,"E2.right"),sQuery(id+"F0.wireOp",EDGE,"E7.3"),sQuery(id+"F0.wireOp",EDGE,"E7.2"),sQuery(id+"F0.wireOp",EDGE,"E19"),sQuery(id+"F0.wireOp",EDGE,"E20"),sQuery(id+"F0.wireOp",EDGE,"E21.0")])],"isStart":false});
            extrude(context, id + "F6", {"entities" : qUnion([Q0, Q1, Q2, Q3]), "operationType" : NewBodyOperationType.ADD, "depth" : 5 * mm, "hasSecondDirection" : true, "secondDirectionOppositeDirection" : false, "secondDirectionDepth" : 2.5 * mm});
        }
        {
            var Q0;
            {var subQ18=sQuery(id+"F0.wireOp",EDGE,"E33.1");Q0=makeQuery(id+"F0.imprint","IMPRINT",FACE,{"disambiguationData":[TD([[makeQuery(id+"F0.imprint","IMPRINT",EDGE,{"derivedFrom":subQ18}),-1.0]])]});}
            var Q1;
            {var subQ0=sQuery(id+"F0.wireOp",EDGE,"E35");Q1=makeQuery(id+"F0.imprint","IMPRINT",FACE,{"disambiguationData":[TD([[makeQuery(id+"F0.imprint","IMPRINT",EDGE,{"derivedFrom":subQ0}),-1.0]])]});}
            extrude(context, id + "F7", {"entities" : qUnion([Q0, Q1]), "operationType" : NewBodyOperationType.ADD, "depth" : 12.5 * mm});
        }
        {
            var Q0;
            {var subQ0=sQuery(id+"F0.wireOp",EDGE,"E35");Q0=makeQuery(id+"F0.imprint","IMPRINT",FACE,{"disambiguationData":[TD([[makeQuery(id+"F0.imprint","IMPRINT",EDGE,{"derivedFrom":subQ0}),-1.0]])]});}
            extrude(context, id + "F8", {"entities" : qUnion([Q0]), "operationType" : NewBodyOperationType.ADD, "depth" : 6.5 * mm});
        }
        {
            var Q0;
            Q0=makeQuery(id+"F0.imprint","IMPRINT",FACE,{"disambiguationData":[TD([[makeQuery(id+"F0.imprint","IMPRINT",EDGE,{"derivedFrom":sQuery(id+"F0.wireOp",EDGE,"E38.bottom")}),1.0]])]});
            extrude(context, id + "F9", {"entities" : qUnion([Q0]), "operationType" : NewBodyOperationType.ADD, "depth" : 1.2 * mm});
        }
        {
            var Q0;
            Q0=makeQuery(id+"F0.imprint","IMPRINT",FACE,{"disambiguationData":[TD([[makeQuery(id+"F0.imprint","IMPRINT",EDGE,{"derivedFrom":sQuery(id+"F0.wireOp",EDGE,"E38.bottom")}),-1.0]])]});
            extrude(context, id + "F10", {"entities" : qUnion([Q0]), "operationType" : NewBodyOperationType.ADD, "depth" : 5 * mm});
        }
        {
            var Q0;
            {var subQ3=sQuery(id+"F0.wireOp",EDGE,"E42");Q0=makeQuery(id+"F0.imprint","IMPRINT",FACE,{"disambiguationData":[TD([[makeQuery(id+"F0.imprint","IMPRINT",EDGE,{"derivedFrom":subQ3}),1.0]])]});}
            var Q1;
            {var subQ3=sQuery(id+"F0.wireOp",EDGE,"E43");Q1=makeQuery(id+"F0.imprint","IMPRINT",FACE,{"disambiguationData":[TD([[makeQuery(id+"F0.imprint","IMPRINT",EDGE,{"derivedFrom":subQ3}),1.0]])]});}
            var Q2;
            {var subQ3=sQuery(id+"F0.wireOp",EDGE,"E40");Q2=makeQuery(id+"F0.imprint","IMPRINT",FACE,{"disambiguationData":[TD([[makeQuery(id+"F0.imprint","IMPRINT",EDGE,{"derivedFrom":subQ3}),1.0]])]});}
            var Q3;
            {var subQ0=sQuery(id+"F0.wireOp",EDGE,"E33.3");var subQ1=sQuery(id+"F0.wireOp",EDGE,"E33.2");var subQ2=makeQuery(id+"F0.imprint","INTERSECT",VERTEX,{"derivedFrom":[subQ1,subQ0]});Q3=makeQuery(id+"F0.imprint","IMPRINT",FACE,{"disambiguationData":[TD([[makeQuery(id+"F0.imprint","IMPRINT",EDGE,{"disambiguationData":[TD([[subQ2,1.0]])],"derivedFrom":subQ1}),1.0]])]});}
            extrude(context, id + "F11", {"entities" : qUnion([Q0, Q1, Q2, Q3]), "operationType" : NewBodyOperationType.ADD, "depth" : 1.2 * mm});
        }
    });
